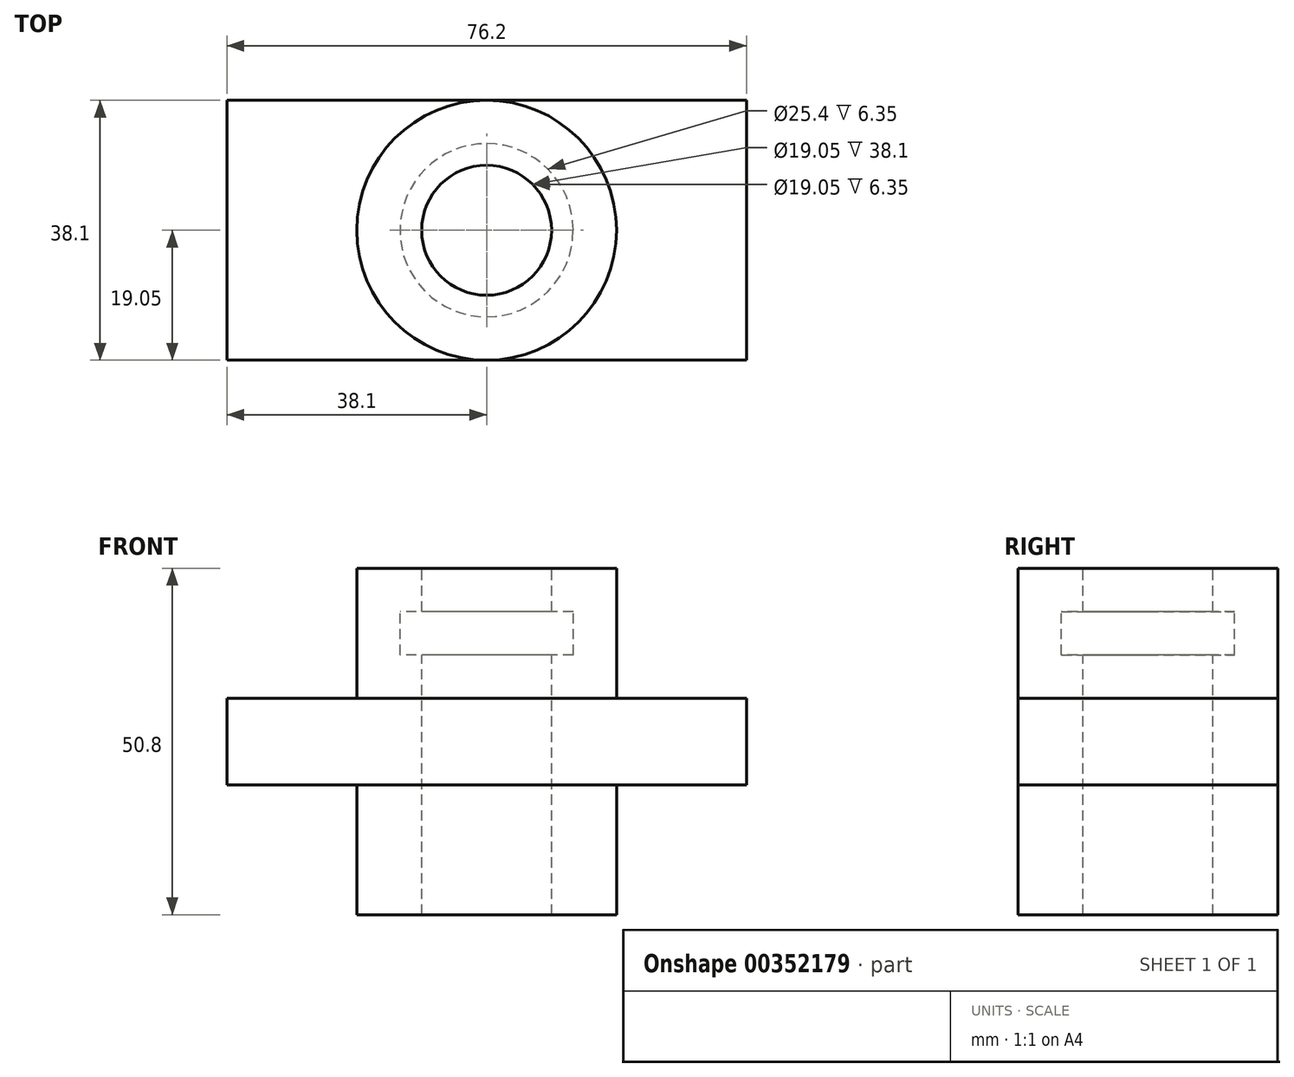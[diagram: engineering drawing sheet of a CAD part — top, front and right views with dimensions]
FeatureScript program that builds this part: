
annotation { "Feature Type Name" : "Feature", "Feature Type Description" : "" }
export const myFeature = defineFeature(function(context is Context, id is Id, definition is map)
    precondition{}
    {
        {
            var Q0;
            Q0=qCreatedBy(makeId("Top.planeOp"),FACE);
            var sketch = newSketch(context, id + "F0", { "sketchPlane" : qUnion([Q0])});
            skLineSegment(sketch, "E0.bottom", {"start": v(-38.1, 19.05) * mm, "end": v(38.1, 19.05) * mm});
            skLineSegment(sketch, "E0.top", {"start": v(-38.1, -19.05) * mm, "end": v(38.1, -19.05) * mm});
            skLineSegment(sketch, "E0.left", {"start": v(-38.1, 19.05) * mm, "end": v(-38.1, -19.05) * mm});
            skLineSegment(sketch, "E0.right", {"start": v(38.1, 19.05) * mm, "end": v(38.1, -19.05) * mm});
            skSolve(sketch);
        }
        {
            var Q0;
            Q0 = qSketchRegion(id + "F0", true);
            extrude(context, id + "F1", {"entities" : qUnion([Q0]), "endBound" : BoundingType.SYMMETRIC, "depth" : 12.7 * mm});
        }
        {
            var Q0;
            Q0=qCreatedBy(makeId("Top.planeOp"),FACE);
            var sketch = newSketch(context, id + "F2", { "sketchPlane" : qUnion([Q0])});
            skCircle(sketch, "E1", {"center": v(0, 0) * mm, "radius": 19.05 * mm});
            skSolve(sketch);
        }
        {
            var Q0;
            Q0 = qSketchRegion(id + "F2", true);
            extrude(context, id + "F3", {"entities" : qUnion([Q0]), "operationType" : NewBodyOperationType.ADD, "endBound" : BoundingType.SYMMETRIC, "depth" : 50.8 * mm});
        }
        {
            var Q0;
            Q0=makeQuery(id+"F3.opExtrude","CAP_FACE",FACE,{"disambiguationData":[OSD([sQuery(id+"F2.wireOp",EDGE,"E1")])],"isStart":false});
            var sketch = newSketch(context, id + "F4", { "sketchPlane" : qUnion([Q0])});
            skCircle(sketch, "E2", {"center": v(0, 0) * mm, "radius": 9.53 * mm});
            skSolve(sketch);
        }
        {
            var Q0;
            Q0 = qSketchRegion(id + "F4", true);
            extrude(context, id + "F5", {"entities" : qUnion([Q0]), "operationType" : NewBodyOperationType.REMOVE, "endBound" : BoundingType.THROUGH_ALL, "oppositeDirection" : true, "depth" : 25.4 * mm});
        }
        {
            var Q0;
            Q0=makeQuery(id+"F3.opExtrude","CAP_FACE",FACE,{"disambiguationData":[OSD([sQuery(id+"F2.wireOp",EDGE,"E1")])],"isStart":false});
            var sketch = newSketch(context, id + "F6", { "sketchPlane" : qUnion([Q0])});
            skCircle(sketch, "E3", {"center": v(0, 0) * mm, "radius": 12.7 * mm});
            skSolve(sketch);
        }
        {
            var Q0;
            Q0 = qSketchRegion(id + "F6", true);
            extrude(context, id + "F7", {"entities" : qUnion([Q0]), "operationType" : NewBodyOperationType.REMOVE, "oppositeDirection" : true, "depth" : 12.7 * mm});
        }
        {
            var Q0;
            Q0=makeQuery(id+"F3.opExtrude","CAP_FACE",FACE,{"disambiguationData":[OSD([sQuery(id+"F2.wireOp",EDGE,"E1")])],"isStart":false});
            var sketch = newSketch(context, id + "F8", { "sketchPlane" : qUnion([Q0])});
            skCircle(sketch, "E4", {"center": v(0, 0) * mm, "radius": 12.7 * mm});
            skSolve(sketch);
        }
        {
            var Q0;
            Q0 = qSketchRegion(id + "F8", true);
            extrude(context, id + "F9", {"entities" : qUnion([Q0]), "operationType" : NewBodyOperationType.ADD, "oppositeDirection" : true, "depth" : 6.35 * mm});
        }
        {
            var Q0;
            Q0=makeQuery(id+"F9.boolean.opBoolean","MERGE",FACE,{"derivedFrom":[makeQuery(id+"F3.opExtrude","CAP_FACE",FACE,{"disambiguationData":[OSD([sQuery(id+"F2.wireOp",EDGE,"E1")])],"isStart":false}),makeQuery(id+"F9.opExtrude","CAP_FACE",FACE,{"disambiguationData":[OSD([sQuery(id+"F8.wireOp",EDGE,"E4")])],"isStart":true})]});
            var sketch = newSketch(context, id + "F10", { "sketchPlane" : qUnion([Q0])});
            skCircle(sketch, "E5", {"center": v(0, 0) * mm, "radius": 9.53 * mm});
            skSolve(sketch);
        }
        {
            var Q0;
            Q0 = qSketchRegion(id + "F10", true);
            extrude(context, id + "F11", {"entities" : qUnion([Q0]), "operationType" : NewBodyOperationType.REMOVE, "endBound" : BoundingType.THROUGH_ALL, "oppositeDirection" : true, "depth" : 25.4 * mm});
        }
    });
